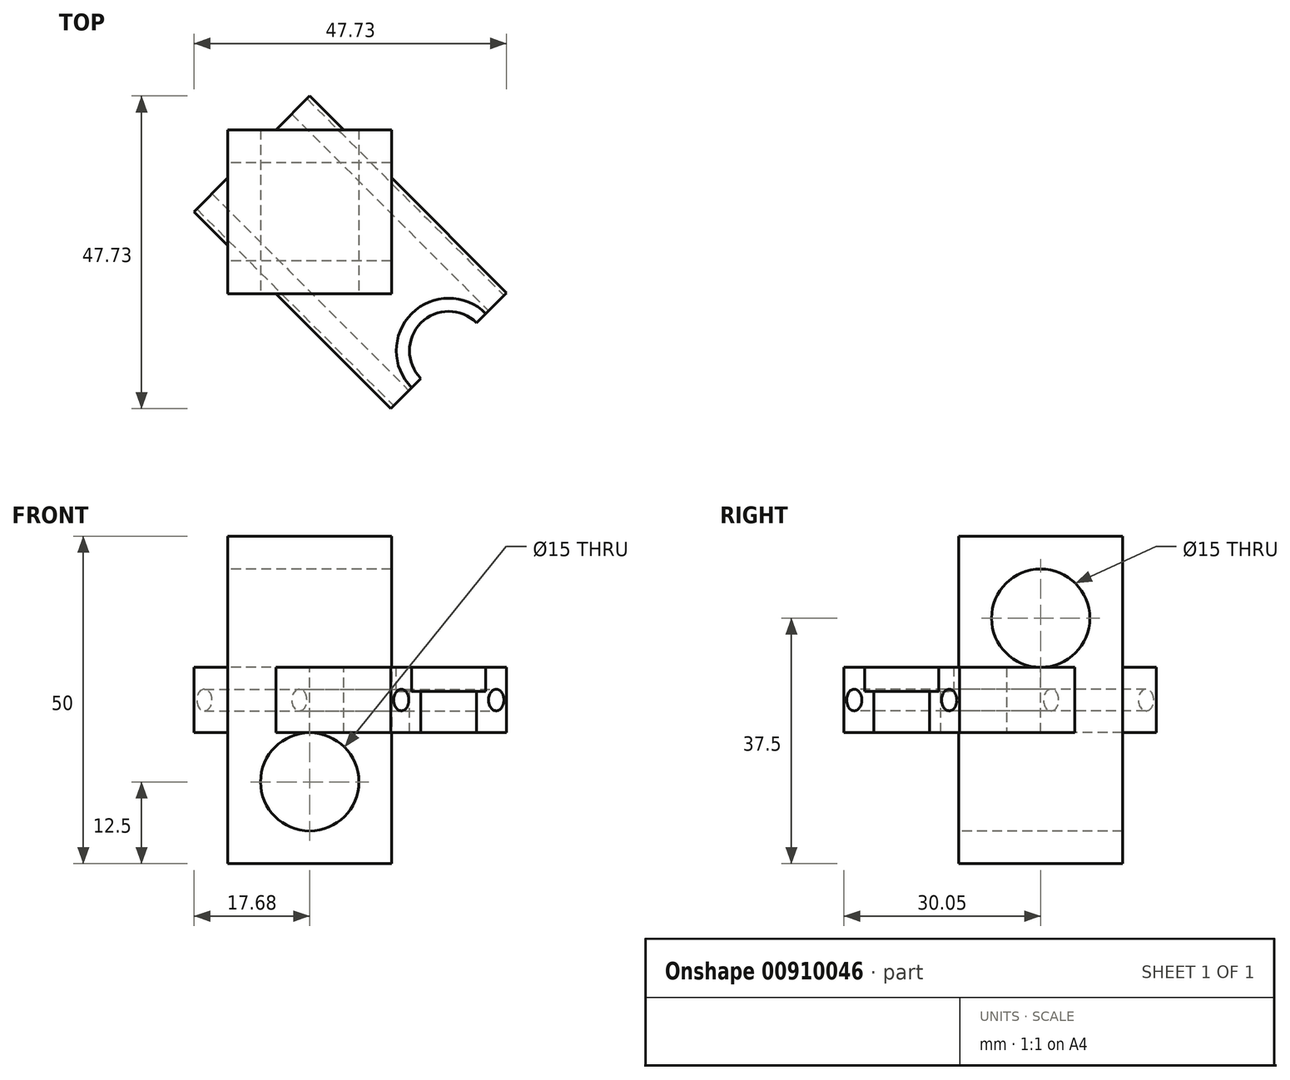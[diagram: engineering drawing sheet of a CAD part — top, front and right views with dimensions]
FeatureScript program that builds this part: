
annotation { "Feature Type Name" : "Feature", "Feature Type Description" : "" }
export const myFeature = defineFeature(function(context is Context, id is Id, definition is map)
    precondition{}
    {
        {
            var Q0;
            Q0=qCreatedBy(makeId("Top.planeOp"),FACE);
            var sketch = newSketch(context, id + "F0", { "sketchPlane" : qUnion([Q0])});
            skLineSegment(sketch, "E0.bottom", {"start": v(0, 0) * mm, "end": v(25, 0) * mm});
            skLineSegment(sketch, "E0.top", {"start": v(0, 25) * mm, "end": v(25, 25) * mm});
            skLineSegment(sketch, "E0.left", {"start": v(0, 0) * mm, "end": v(0, 25) * mm});
            skLineSegment(sketch, "E0.right", {"start": v(25, 0) * mm, "end": v(25, 25) * mm});
            skSolve(sketch);
        }
        {
            var Q0;
            Q0=makeQuery(id+"F0.imprint","IMPRINT",FACE,{"disambiguationData":[TD([[makeQuery(id+"F0.imprint","IMPRINT",EDGE,{"derivedFrom":sQuery(id+"F0.wireOp",EDGE,"E0.bottom")}),1.0]])]});
            extrude(context, id + "F1", {"entities" : qUnion([Q0]), "depth" : 50 * mm, "offsetDistance" : 25 * mm});
        }
        {
            var Q0;
            Q0=makeQuery(id+"F1.opExtrude","SWEPT_FACE",FACE,{"disambiguationData":[OSD([sQuery(id+"F0.wireOp",EDGE,"E0.bottom")])]});
            var sketch = newSketch(context, id + "F2", { "sketchPlane" : qUnion([Q0])});
            skLineSegment(sketch, "E1", {"start": v(12.5, 0) * mm, "end": v(12.5, 12.5) * mm});
            skCircle(sketch, "E2", {"center": v(12.5, 12.5) * mm, "radius": 7.5 * mm});
            skSolve(sketch);
        }
        {
            var Q0;
            Q0=makeQuery(id+"F2.imprint","IMPRINT",FACE,{"disambiguationData":[TD([[makeQuery(id+"F2.imprint","IMPRINT",EDGE,{"derivedFrom":sQuery(id+"F2.wireOp",EDGE,"E2")}),1.0]])]});
            extrude(context, id + "F3", {"entities" : qUnion([Q0]), "operationType" : NewBodyOperationType.REMOVE, "oppositeDirection" : true, "depth" : 25 * mm, "offsetDistance" : 25 * mm});
        }
        {
            var Q0;
            Q0=makeQuery(id+"F1.opExtrude","SWEPT_FACE",FACE,{"disambiguationData":[OSD([sQuery(id+"F0.wireOp",EDGE,"E0.left")])]});
            var sketch = newSketch(context, id + "F4", { "sketchPlane" : qUnion([Q0])});
            skLineSegment(sketch, "E3", {"start": v(-12.5, 50) * mm, "end": v(-12.5, 37.5) * mm});
            skCircle(sketch, "E4", {"center": v(-12.5, 37.5) * mm, "radius": 7.5 * mm});
            skSolve(sketch);
        }
        {
            var Q0;
            Q0=makeQuery(id+"F4.imprint","IMPRINT",FACE,{"disambiguationData":[TD([[makeQuery(id+"F4.imprint","IMPRINT",EDGE,{"derivedFrom":sQuery(id+"F4.wireOp",EDGE,"E4")}),1.0]])]});
            extrude(context, id + "F5", {"entities" : qUnion([Q0]), "operationType" : NewBodyOperationType.REMOVE, "oppositeDirection" : true, "depth" : 25 * mm, "offsetDistance" : 25 * mm});
        }
        {
            var Q0;
            Q0=makeQuery(id+"F1.opExtrude","CAP_FACE",FACE,{"disambiguationData":[OSD([sQuery(id+"F0.wireOp",EDGE,"E0.bottom"),sQuery(id+"F0.wireOp",EDGE,"E0.top"),sQuery(id+"F0.wireOp",EDGE,"E0.left"),sQuery(id+"F0.wireOp",EDGE,"E0.right")])],"isStart":false});
            var sketch = newSketch(context, id + "F6", { "sketchPlane" : qUnion([Q0])});
            skLineSegment(sketch, "E5", {"start": v(0, 0) * mm, "end": v(12.5, 12.5) * mm});
            skPoint(sketch, "E5.endSnap0", {"position": v(12.5, 0) * mm});
            skPoint(sketch, "E5.endSnap1", {"position": v(0, 12.5) * mm});
            skLineSegment(sketch, "E6", {"start": v(12.5, 12.5) * mm, "end": v(3.66, 3.66) * mm});
            skLineSegment(sketch, "E7", {"start": v(3.66, 3.66) * mm, "end": v(-5.18, 12.5) * mm});
            skLineSegment(sketch, "E8", {"start": v(-5.18, 12.5) * mm, "end": v(12.5, 30.18) * mm});
            skLineSegment(sketch, "E9", {"start": v(12.5, 30.18) * mm, "end": v(30.18, 12.5) * mm});
            skLineSegment(sketch, "E10", {"start": v(30.18, 12.5) * mm, "end": v(12.5, -5.18) * mm});
            skLineSegment(sketch, "E11", {"start": v(12.5, -5.18) * mm, "end": v(3.66, 3.66) * mm});
            skSolve(sketch);
        }
        {
            var Q0;
            {var subQ0=sQuery(id+"F6.wireOp",EDGE,"E8");var subQ1=sQuery(id+"F6.wireOp",EDGE,"E7");var subQ2=makeQuery(id+"F6.imprint","INTERSECT",VERTEX,{"derivedFrom":[subQ1,subQ0]});Q0=makeQuery(id+"F6.imprint","IMPRINT",FACE,{"disambiguationData":[TD([[makeQuery(id+"F6.imprint","IMPRINT",EDGE,{"disambiguationData":[TD([[subQ2,1.0]])],"derivedFrom":subQ1}),-1.0]])]});}
            var Q1;
            {var subQ9=sQuery(id+"F6.wireOp",EDGE,"E8");var subQ10=makeQuery(id+"F1.opExtrude","CAP_EDGE",EDGE,{"disambiguationData":[OSD([sQuery(id+"F0.wireOp",EDGE,"E0.left")])],"isStart":false});var subQ11=makeQuery(id+"F6.imprint","INTERSECT",VERTEX,{"derivedFrom":[subQ10,subQ9]});Q1=makeQuery(id+"F6.imprint","IMPRINT",FACE,{"disambiguationData":[TD([[makeQuery(id+"F6.imprint","IMPRINT",EDGE,{"disambiguationData":[TD([[subQ11,-1.0]])],"derivedFrom":subQ9}),-1.0]])]});}
            var Q2;
            {var subQ0=sQuery(id+"F6.wireOp",EDGE,"E9");var subQ1=sQuery(id+"F6.wireOp",EDGE,"E8");var subQ2=makeQuery(id+"F6.imprint","INTERSECT",VERTEX,{"derivedFrom":[subQ1,subQ0]});Q2=makeQuery(id+"F6.imprint","IMPRINT",FACE,{"disambiguationData":[TD([[makeQuery(id+"F6.imprint","IMPRINT",EDGE,{"disambiguationData":[TD([[subQ2,1.0]])],"derivedFrom":subQ1}),-1.0]])]});}
            var Q3;
            {var subQ0=sQuery(id+"F6.wireOp",EDGE,"E10");var subQ1=sQuery(id+"F6.wireOp",EDGE,"E9");var subQ2=makeQuery(id+"F6.imprint","INTERSECT",VERTEX,{"derivedFrom":[subQ1,subQ0]});Q3=makeQuery(id+"F6.imprint","IMPRINT",FACE,{"disambiguationData":[TD([[makeQuery(id+"F6.imprint","IMPRINT",EDGE,{"disambiguationData":[TD([[subQ2,1.0]])],"derivedFrom":subQ1}),-1.0]])]});}
            var Q4;
            {var subQ0=sQuery(id+"F6.wireOp",EDGE,"E11");var subQ1=sQuery(id+"F6.wireOp",EDGE,"E10");var subQ2=makeQuery(id+"F6.imprint","INTERSECT",VERTEX,{"derivedFrom":[subQ1,subQ0]});Q4=makeQuery(id+"F6.imprint","IMPRINT",FACE,{"disambiguationData":[TD([[makeQuery(id+"F6.imprint","IMPRINT",EDGE,{"disambiguationData":[TD([[subQ2,1.0]])],"derivedFrom":subQ1}),-1.0]])]});}
            extrude(context, id + "F7", {"entities" : qUnion([Q0, Q1, Q2, Q3, Q4]), "operationType" : NewBodyOperationType.ADD, "oppositeDirection" : true, "depth" : 30 * mm, "offsetDistance" : 25 * mm, "hasSecondDirection" : true, "secondDirectionOppositeDirection" : true, "secondDirectionDepth" : 20 * mm});
        }
        {
            var Q0;
            {var subQ1=sQuery(id+"F6.wireOp",EDGE,"E10");Q0=makeQuery(id+"F7.boolean.opBoolean","SPLIT",FACE,{"disambiguationData":[TD([makeQuery(id+"F1.opExtrude","SWEPT_FACE",FACE,{"disambiguationData":[OSD([sQuery(id+"F0.wireOp",EDGE,"E0.bottom")])]})])],"derivedFrom":makeQuery(id+"F7.opExtrude","SWEPT_FACE",FACE,{"disambiguationData":[OSD([subQ1])]})});}
            var Q1;
            {var subQ2=sQuery(id+"F6.wireOp",EDGE,"E10");Q1=makeQuery(id+"F7.boolean.opBoolean","SPLIT",FACE,{"disambiguationData":[TD([makeQuery(id+"F1.opExtrude","SWEPT_FACE",FACE,{"disambiguationData":[OSD([sQuery(id+"F0.wireOp",EDGE,"E0.right")])]})])],"derivedFrom":makeQuery(id+"F7.opExtrude","SWEPT_FACE",FACE,{"disambiguationData":[OSD([subQ2])]})});}
            extrude(context, id + "F8", {"entities" : qUnion([Q0, Q1]), "operationType" : NewBodyOperationType.ADD, "depth" : 30 * mm, "offsetDistance" : 25 * mm});
        }
        {
            var Q0;
            Q0=makeQuery(id+"F8.opExtrude","SWEPT_FACE",FACE,{"disambiguationData":[OSD([sQuery(id+"F0.wireOp",EDGE,"E0.right"),sQuery(id+"F6.wireOp",EDGE,"E10")])]});
            extrude(context, id + "F9", {"entities" : qUnion([Q0]), "operationType" : NewBodyOperationType.ADD, "depth" : 12.5 * mm, "offsetDistance" : 25 * mm});
        }
        {
            var Q0;
            {var subQ0=sQuery(id+"F6.wireOp",EDGE,"E10");var subQ1=sQuery(id+"F0.wireOp",EDGE,"E0.right");var subQ8=makeQuery(id+"F7.opExtrude","SWEPT_FACE",FACE,{"disambiguationData":[OSD([subQ0])]});Q0=makeQuery(id+"F9.boolean.opBoolean","MERGE",FACE,{"derivedFrom":[makeQuery(id+"F8.opExtrude","CAP_FACE",FACE,{"disambiguationData":[OSD([subQ0]),TDD([makeQuery(id+"F7.boolean.opBoolean","SPLIT",FACE,{"disambiguationData":[TD([makeQuery(id+"F1.opExtrude","SWEPT_FACE",FACE,{"disambiguationData":[OSD([subQ1])]})])],"derivedFrom":subQ8})])],"isStart":false}),makeQuery(id+"F8.opExtrude","CAP_FACE",FACE,{"disambiguationData":[OSD([subQ0]),TDD([makeQuery(id+"F7.boolean.opBoolean","SPLIT",FACE,{"disambiguationData":[TD([makeQuery(id+"F1.opExtrude","SWEPT_FACE",FACE,{"disambiguationData":[OSD([sQuery(id+"F0.wireOp",EDGE,"E0.bottom")])]})])],"derivedFrom":subQ8})])],"isStart":false}),makeQuery(id+"F9.opExtrude","SWEPT_FACE",FACE,{"disambiguationData":[OSD([subQ1,subQ0]),TDD([makeQuery(id+"F8.opExtrude","CAP_EDGE",EDGE,{"disambiguationData":[OSD([subQ1,subQ0])],"isStart":false})])]})]});}
            extrude(context, id + "F10", {"entities" : qUnion([Q0]), "operationType" : NewBodyOperationType.REMOVE, "oppositeDirection" : true, "depth" : 12.5 * mm, "offsetDistance" : 25 * mm});
        }
        {
            var Q0;
            {var subQ0=sQuery(id+"F6.wireOp",EDGE,"E10");var subQ1=makeQuery(id+"F7.opExtrude","SWEPT_FACE",FACE,{"disambiguationData":[OSD([subQ0])]});var subQ2=sQuery(id+"F6.wireOp",EDGE,"E11");var subQ3=sQuery(id+"F6.wireOp",EDGE,"E9");var subQ4=sQuery(id+"F6.wireOp",EDGE,"E8");var subQ5=sQuery(id+"F6.wireOp",EDGE,"E7");var subQ6=makeQuery(id+"F7.opExtrude","CAP_FACE",FACE,{"disambiguationData":[OSD([subQ5,subQ4,subQ3,subQ0,subQ2])],"isStart":true});var subQ7=sQuery(id+"F0.wireOp",EDGE,"E0.right");var subQ8=makeQuery(id+"F1.opExtrude","SWEPT_FACE",FACE,{"disambiguationData":[OSD([subQ7])]});var subQ10=makeQuery(id+"F7.opExtrude","CAP_EDGE",EDGE,{"disambiguationData":[OSD([subQ0])],"isStart":true});var subQ11=makeQuery(id+"F1.opExtrude","SWEPT_FACE",FACE,{"disambiguationData":[OSD([sQuery(id+"F0.wireOp",EDGE,"E0.bottom")])]});Q0=makeQuery(id+"F9.boolean.opBoolean","MERGE",FACE,{"derivedFrom":[makeQuery(id+"F8.boolean.opBoolean","MERGE",FACE,{"derivedFrom":[makeQuery(id+"F7.boolean.opBoolean","SPLIT",FACE,{"disambiguationData":[TD([subQ11])],"derivedFrom":subQ6}),makeQuery(id+"F8.opExtrude","SWEPT_FACE",FACE,{"disambiguationData":[OSD([subQ0]),TDD([makeQuery(id+"F7.boolean.opBoolean","SPLIT",EDGE,{"disambiguationData":[TD([subQ11])],"derivedFrom":subQ10})])]})]}),makeQuery(id+"F8.boolean.opBoolean","MERGE",FACE,{"derivedFrom":[makeQuery(id+"F7.boolean.opBoolean","SPLIT",FACE,{"disambiguationData":[TD([subQ8])],"derivedFrom":subQ6}),makeQuery(id+"F8.opExtrude","SWEPT_FACE",FACE,{"disambiguationData":[OSD([subQ0]),TDD([makeQuery(id+"F7.boolean.opBoolean","SPLIT",EDGE,{"disambiguationData":[TD([subQ8])],"derivedFrom":subQ10})])]})]}),makeQuery(id+"F9.opExtrude","SWEPT_FACE",FACE,{"disambiguationData":[OSD([subQ7,subQ5,subQ4,subQ3,subQ0,subQ2]),TDD([makeQuery(id+"F8.opExtrude","SWEPT_EDGE",EDGE,{"disambiguationData":[OSD([subQ7,subQ5,subQ4,subQ3,subQ0,subQ2]),TDD([makeQuery(id+"F7.boolean.opBoolean","INTERSECT",VERTEX,{"derivedFrom":[subQ8,subQ6,subQ1]})])]})])]})]});}
            var sketch = newSketch(context, id + "F11", { "sketchPlane" : qUnion([Q0])});
            skLineSegment(sketch, "E12", {"start": v(33.71, -8.71) * mm, "end": v(26.64, -1.64) * mm});
            skCircle(sketch, "E13", {"center": v(33.71, -8.71) * mm, "radius": 8 * mm});
            skCircle(sketch, "E14", {"center": v(33.71, -8.71) * mm, "radius": 6 * mm});
            skSolve(sketch);
        }
        {
            var Q0;
            {var subQ0=sQuery(id+"F11.wireOp",EDGE,"E12");var subQ13=sQuery(id+"F11.wireOp",EDGE,"E14");var subQ14=makeQuery(id+"F11.imprint","INTERSECT",VERTEX,{"derivedFrom":[subQ0,subQ13]});Q0=makeQuery(id+"F11.imprint","IMPRINT",FACE,{"disambiguationData":[TD([[makeQuery(id+"F11.imprint","IMPRINT",EDGE,{"disambiguationData":[TD([[subQ14,1.0]])],"derivedFrom":subQ0}),1.0]])]});}
            var Q1;
            {var subQ0=sQuery(id+"F11.wireOp",EDGE,"E13");var subQ1=sQuery(id+"F11.wireOp",EDGE,"E12");var subQ2=makeQuery(id+"F11.imprint","INTERSECT",VERTEX,{"derivedFrom":[subQ1,subQ0]});Q1=makeQuery(id+"F11.imprint","IMPRINT",FACE,{"disambiguationData":[TD([[makeQuery(id+"F11.imprint","IMPRINT",EDGE,{"disambiguationData":[TD([[subQ2,1.0]])],"derivedFrom":subQ1}),1.0]])]});}
            var Q2;
            {var subQ0=sQuery(id+"F11.wireOp",EDGE,"E12");var subQ13=sQuery(id+"F11.wireOp",EDGE,"E14");var subQ14=makeQuery(id+"F11.imprint","INTERSECT",VERTEX,{"derivedFrom":[subQ0,subQ13]});Q2=makeQuery(id+"F11.imprint","IMPRINT",FACE,{"disambiguationData":[TD([[makeQuery(id+"F11.imprint","IMPRINT",EDGE,{"disambiguationData":[TD([[subQ14,1.0]])],"derivedFrom":subQ0}),-1.0]])]});}
            var Q3;
            {var subQ0=sQuery(id+"F11.wireOp",EDGE,"E13");var subQ1=sQuery(id+"F11.wireOp",EDGE,"E12");var subQ2=makeQuery(id+"F11.imprint","INTERSECT",VERTEX,{"derivedFrom":[subQ1,subQ0]});Q3=makeQuery(id+"F11.imprint","IMPRINT",FACE,{"disambiguationData":[TD([[makeQuery(id+"F11.imprint","IMPRINT",EDGE,{"disambiguationData":[TD([[subQ2,1.0]])],"derivedFrom":subQ1}),-1.0]])]});}
            extrude(context, id + "F12", {"entities" : qUnion([Q0, Q1, Q2, Q3]), "operationType" : NewBodyOperationType.REMOVE, "oppositeDirection" : true, "depth" : 10 * mm, "offsetDistance" : 25 * mm});
        }
        {
            var Q0;
            {var subQ0=sQuery(id+"F11.wireOp",EDGE,"E14");var subQ1=sQuery(id+"F11.wireOp",EDGE,"E12");var subQ2=makeQuery(id+"F11.imprint","INTERSECT",VERTEX,{"derivedFrom":[subQ1,subQ0]});Q0=makeQuery(id+"F11.imprint","IMPRINT",FACE,{"disambiguationData":[TD([[makeQuery(id+"F11.imprint","IMPRINT",EDGE,{"disambiguationData":[TD([[subQ2,-1.0]])],"derivedFrom":subQ1}),1.0]])]});}
            var Q1;
            {var subQ0=sQuery(id+"F11.wireOp",EDGE,"E14");var subQ1=sQuery(id+"F11.wireOp",EDGE,"E12");var subQ2=makeQuery(id+"F11.imprint","INTERSECT",VERTEX,{"derivedFrom":[subQ1,subQ0]});Q1=makeQuery(id+"F11.imprint","IMPRINT",FACE,{"disambiguationData":[TD([[makeQuery(id+"F11.imprint","IMPRINT",EDGE,{"disambiguationData":[TD([[subQ2,-1.0]])],"derivedFrom":subQ1}),-1.0]])]});}
            extrude(context, id + "F13", {"entities" : qUnion([Q0, Q1]), "operationType" : NewBodyOperationType.ADD, "oppositeDirection" : true, "depth" : 10 * mm, "offsetDistance" : 25 * mm});
        }
        {
            var Q0;
            {var subQ0=sQuery(id+"F11.wireOp",EDGE,"E13");var subQ1=sQuery(id+"F6.wireOp",EDGE,"E10");var subQ2=makeQuery(id+"F7.opExtrude","SWEPT_FACE",FACE,{"disambiguationData":[OSD([subQ1])]});var subQ3=sQuery(id+"F6.wireOp",EDGE,"E11");var subQ4=sQuery(id+"F6.wireOp",EDGE,"E9");var subQ5=sQuery(id+"F6.wireOp",EDGE,"E8");var subQ6=sQuery(id+"F6.wireOp",EDGE,"E7");var subQ7=makeQuery(id+"F7.opExtrude","CAP_FACE",FACE,{"disambiguationData":[OSD([subQ6,subQ5,subQ4,subQ1,subQ3])],"isStart":true});var subQ8=sQuery(id+"F0.wireOp",EDGE,"E0.right");var subQ9=makeQuery(id+"F1.opExtrude","SWEPT_FACE",FACE,{"disambiguationData":[OSD([subQ8])]});var subQ10=subQ9;var subQ11=makeQuery(id+"F7.boolean.opBoolean","INTERSECT",VERTEX,{"derivedFrom":[subQ10,subQ7,subQ2]});var subQ12=makeQuery(id+"F1.opExtrude","SWEPT_FACE",FACE,{"disambiguationData":[OSD([sQuery(id+"F0.wireOp",EDGE,"E0.bottom")])]});var subQ13=makeQuery(id+"F7.opExtrude","SWEPT_FACE",FACE,{"disambiguationData":[OSD([subQ6,subQ3])]});var subQ14=makeQuery(id+"F7.opExtrude","CAP_EDGE",EDGE,{"disambiguationData":[OSD([subQ1])],"isStart":true});var subQ15=makeQuery(id+"F7.boolean.opBoolean","SPLIT",EDGE,{"disambiguationData":[TD([subQ12])],"derivedFrom":subQ14});var subQ17=makeQuery(id+"F7.boolean.opBoolean","SPLIT",EDGE,{"disambiguationData":[TD([subQ9])],"derivedFrom":subQ14});var subQ18=makeQuery(id+"F10.boolean.opBoolean","COPY",EDGE,{"derivedFrom":makeQuery(id+"F10.opExtrude","CAP_EDGE",EDGE,{"disambiguationData":[OSD([subQ8,subQ6,subQ5,subQ4,subQ1,subQ3]),TDD([makeQuery(id+"F9.boolean.opBoolean","MERGE",EDGE,{"derivedFrom":[makeQuery(id+"F8.opExtrude","CAP_EDGE",EDGE,{"disambiguationData":[OSD([subQ1]),TDD([subQ17])],"isStart":false}),makeQuery(id+"F8.opExtrude","CAP_EDGE",EDGE,{"disambiguationData":[OSD([subQ1]),TDD([subQ15])],"isStart":false}),makeQuery(id+"F9.opExtrude","SWEPT_EDGE",EDGE,{"disambiguationData":[OSD([subQ8,subQ6,subQ5,subQ4,subQ1,subQ3]),TDD([makeQuery(id+"F8.opExtrude","CAP_VERTEX",VERTEX,{"disambiguationData":[OSD([subQ8,subQ6,subQ5,subQ4,subQ1,subQ3]),TDD([subQ11])],"isStart":false})])]})]})])],"isStart":false})});Q0=makeQuery(id+"F13.boolean.opBoolean","MERGE",FACE,{"derivedFrom":[makeQuery(id+"F12.boolean.opBoolean","SPLIT",FACE,{"disambiguationData":[TD([subQ13])],"derivedFrom":makeQuery(id+"F10.boolean.opBoolean","COPY",FACE,{"derivedFrom":makeQuery(id+"F10.opExtrude","CAP_FACE",FACE,{"disambiguationData":[OSD([subQ8,subQ1])],"isStart":false})})}),makeQuery(id+"F13.opExtrude","SWEPT_FACE",FACE,{"disambiguationData":[OSD([subQ8,subQ6,subQ5,subQ4,subQ1,subQ3]),TDD([makeQuery(id+"F11.imprint","IMPRINT",EDGE,{"disambiguationData":[TD([[makeQuery(id+"F11.imprint","INTERSECT",VERTEX,{"disambiguationData":[OD(1.0)],"derivedFrom":[subQ18,subQ0]}),1.0]])],"derivedFrom":subQ18})])]})]});}
            var sketch = newSketch(context, id + "F14", { "sketchPlane" : qUnion([Q0])});
            skLineSegment(sketch, "E15", {"start": v(5.18, 25) * mm, "end": v(30.18, 25) * mm});
            skLineSegment(sketch, "E16", {"start": v(17.68, 25) * mm, "end": v(7.43, 25) * mm});
            skCircle(sketch, "E17", {"center": v(7.43, 25) * mm, "radius": 1.65 * mm});
            skLineSegment(sketch, "E18", {"start": v(17.68, 25) * mm, "end": v(27.93, 25) * mm});
            skCircle(sketch, "E19", {"center": v(27.93, 25) * mm, "radius": 1.65 * mm});
            skSolve(sketch);
        }
        {
            var Q0;
            {var subQ1=sQuery(id+"F14.wireOp",EDGE,"E15");var subQ3=makeQuery(id+"F14.imprint","IMPRINT",VERTEX,{"disambiguationData":[OD(1.0)],"derivedFrom":subQ1});Q0=makeQuery(id+"F14.imprint","IMPRINT",FACE,{"disambiguationData":[TD([[makeQuery(id+"F14.imprint","IMPRINT",EDGE,{"disambiguationData":[TD([[subQ3,-1.0]])],"derivedFrom":subQ1}),-1.0]])]});}
            var Q1;
            {var subQ1=sQuery(id+"F14.wireOp",EDGE,"E15");var subQ3=makeQuery(id+"F14.imprint","IMPRINT",VERTEX,{"disambiguationData":[OD(1.0)],"derivedFrom":subQ1});Q1=makeQuery(id+"F14.imprint","IMPRINT",FACE,{"disambiguationData":[TD([[makeQuery(id+"F14.imprint","IMPRINT",EDGE,{"disambiguationData":[TD([[subQ3,-1.0]])],"derivedFrom":subQ1}),1.0]])]});}
            var Q2;
            {var subQ0=sQuery(id+"F14.wireOp",EDGE,"E15");var subQ1=makeQuery(id+"F14.imprint","IMPRINT",VERTEX,{"disambiguationData":[OD(0.0)],"derivedFrom":subQ0});Q2=makeQuery(id+"F14.imprint","IMPRINT",FACE,{"disambiguationData":[TD([[makeQuery(id+"F14.imprint","IMPRINT",EDGE,{"disambiguationData":[TD([[subQ1,1.0]])],"derivedFrom":subQ0}),-1.0]])]});}
            var Q3;
            {var subQ0=sQuery(id+"F14.wireOp",EDGE,"E15");var subQ1=makeQuery(id+"F14.imprint","IMPRINT",VERTEX,{"disambiguationData":[OD(0.0)],"derivedFrom":subQ0});Q3=makeQuery(id+"F14.imprint","IMPRINT",FACE,{"disambiguationData":[TD([[makeQuery(id+"F14.imprint","IMPRINT",EDGE,{"disambiguationData":[TD([[subQ1,1.0]])],"derivedFrom":subQ0}),1.0]])]});}
            extrude(context, id + "F15", {"entities" : qUnion([Q0, Q1, Q2, Q3]), "operationType" : NewBodyOperationType.REMOVE, "oppositeDirection" : true, "depth" : 53.1 * mm, "offsetDistance" : 25 * mm});
        }
        {
            var Q0;
            {var subQ0=sQuery(id+"F11.wireOp",EDGE,"E14");var subQ1=sQuery(id+"F11.wireOp",EDGE,"E12");var subQ2=makeQuery(id+"F11.imprint","INTERSECT",VERTEX,{"derivedFrom":[subQ1,subQ0]});Q0=makeQuery(id+"F11.imprint","IMPRINT",FACE,{"disambiguationData":[TD([[makeQuery(id+"F11.imprint","IMPRINT",EDGE,{"disambiguationData":[TD([[subQ2,-1.0]])],"derivedFrom":subQ1}),1.0]])]});}
            var Q1;
            {var subQ0=sQuery(id+"F11.wireOp",EDGE,"E14");var subQ1=sQuery(id+"F11.wireOp",EDGE,"E12");var subQ2=makeQuery(id+"F11.imprint","INTERSECT",VERTEX,{"derivedFrom":[subQ1,subQ0]});Q1=makeQuery(id+"F11.imprint","IMPRINT",FACE,{"disambiguationData":[TD([[makeQuery(id+"F11.imprint","IMPRINT",EDGE,{"disambiguationData":[TD([[subQ2,-1.0]])],"derivedFrom":subQ1}),-1.0]])]});}
            extrude(context, id + "F16", {"entities" : qUnion([Q0, Q1]), "operationType" : NewBodyOperationType.REMOVE, "oppositeDirection" : true, "depth" : 3.7 * mm, "offsetDistance" : 25 * mm});
        }
    });
